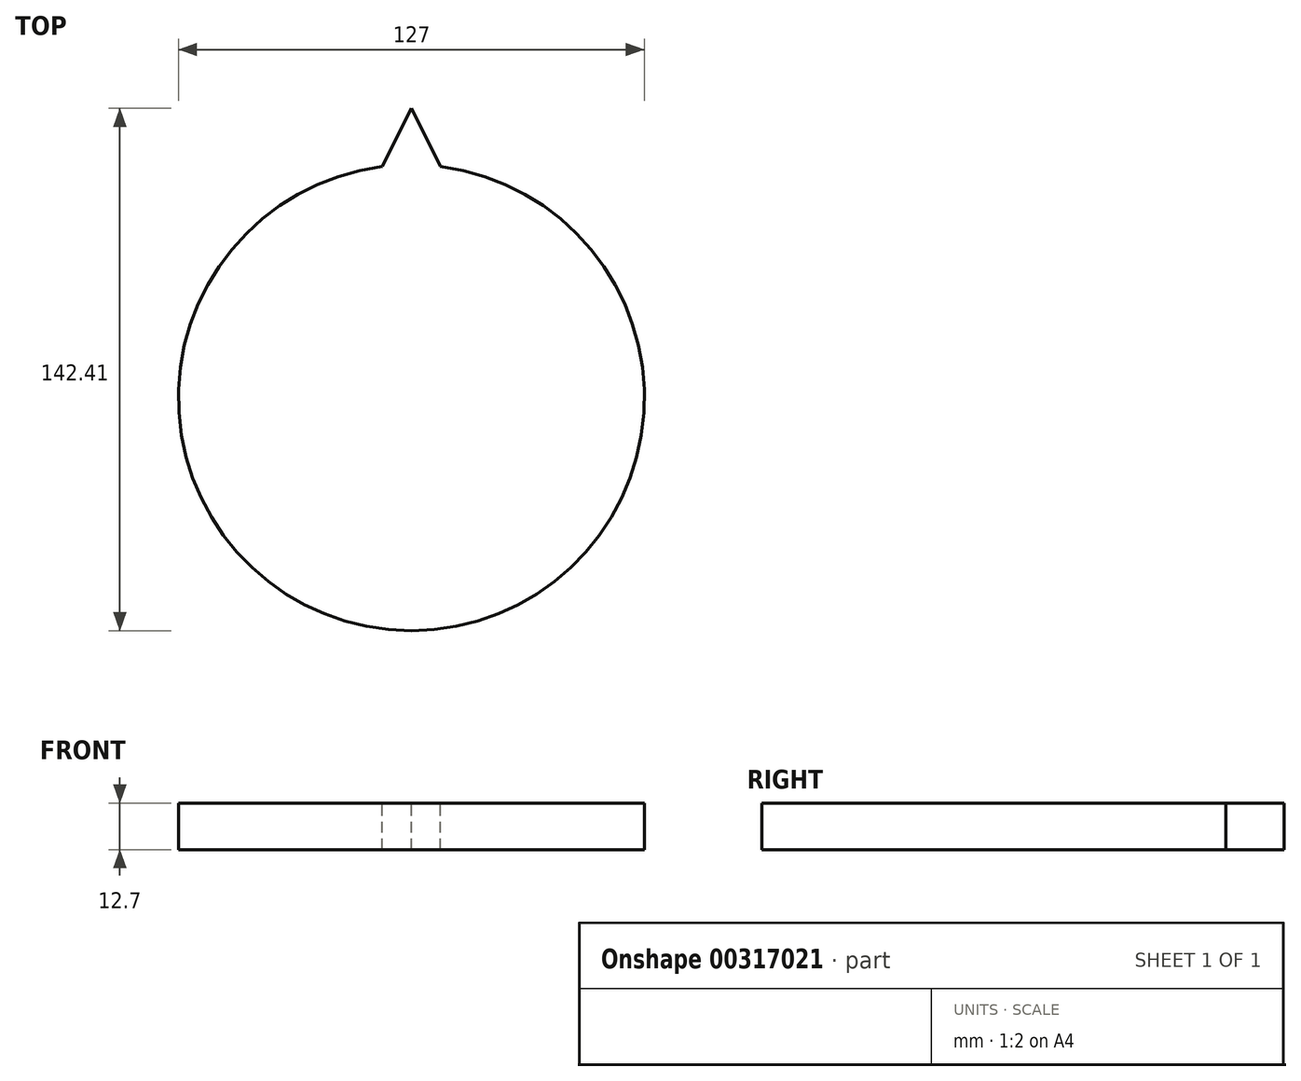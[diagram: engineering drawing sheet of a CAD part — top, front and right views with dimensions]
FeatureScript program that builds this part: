
annotation { "Feature Type Name" : "Feature", "Feature Type Description" : "" }
export const myFeature = defineFeature(function(context is Context, id is Id, definition is map)
    precondition{}
    {
        {
            var Q0;
            Q0=qCreatedBy(makeId("Top.planeOp"),FACE);
            var sketch = newSketch(context, id + "F0", { "sketchPlane" : qUnion([Q0])});
            skCircle(sketch, "E0", {"center": v(0, 0) * mm, "radius": 63.5 * mm});
            skSolve(sketch);
        }
        {
            var Q0;
            Q0 = qSketchRegion(id + "F0", true);
            extrude(context, id + "F1", {"entities" : qUnion([Q0]), "depth" : 12.7 * mm, "symmetric" : true});
        }
        {
            var Q0;
            Q0=makeQuery(id+"F1.opExtrude","CAP_FACE",FACE,{"disambiguationData":[OSD([sQuery(id+"F0.wireOp",EDGE,"E0")])],"isStart":false});
            var sketch = newSketch(context, id + "F2", { "sketchPlane" : qUnion([Q0])});
            skLineSegment(sketch, "E1", {"start": v(-7.94, 63) * mm, "end": v(0, 78.91) * mm});
            skLineSegment(sketch, "E2", {"start": v(0, 78.91) * mm, "end": v(7.94, 63) * mm});
            skArc(sketch, "E3.0", {"start": v(7.94, 63) * mm, "mid": v(0, 63.5) * mm, "end": v(-7.94, 63) * mm});
            skSolve(sketch);
        }
        {
            var Q0;
            Q0 = qSketchRegion(id + "F2", true);
            var Q1;
            Q1=makeQuery(id+"F1.opExtrude","CAP_FACE",FACE,{"disambiguationData":[OSD([sQuery(id+"F0.wireOp",EDGE,"E0")])],"isStart":true});
            extrude(context, id + "F3", {"entities" : qUnion([Q0]), "operationType" : NewBodyOperationType.ADD, "endBound" : BoundingType.UP_TO_SURFACE, "oppositeDirection" : true, "endBoundEntityFace" : qUnion([Q1]), "depth" : 25.4 * mm});
        }
    });
